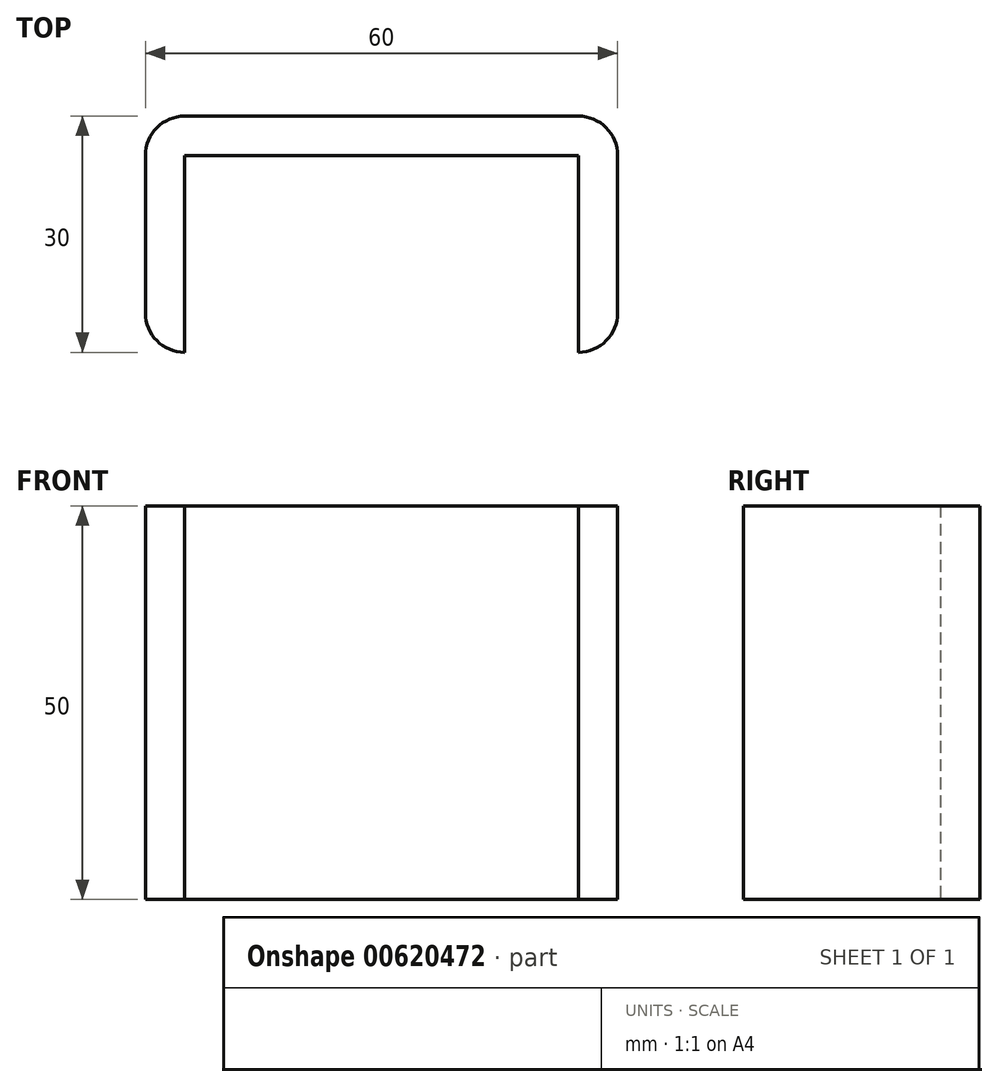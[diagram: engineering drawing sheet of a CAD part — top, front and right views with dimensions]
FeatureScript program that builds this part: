
annotation { "Feature Type Name" : "Feature", "Feature Type Description" : "" }
export const myFeature = defineFeature(function(context is Context, id is Id, definition is map)
    precondition{}
    {
        {
            var Q0;
            Q0=qCreatedBy(makeId("Top.planeOp"),FACE);
            var sketch = newSketch(context, id + "F0", { "sketchPlane" : qUnion([Q0])});
            skLineSegment(sketch, "E0.bottom", {"start": v(-30, 15) * mm, "end": v(30, 15) * mm});
            skLineSegment(sketch, "E0.top", {"start": v(-30, -15) * mm, "end": v(-25, -15) * mm});
            skLineSegment(sketch, "E0.left", {"start": v(-30, 15) * mm, "end": v(-30, -15) * mm});
            skLineSegment(sketch, "E0.right", {"start": v(30, 15) * mm, "end": v(30, -15) * mm});
            skPoint(sketch, "E0.middle", {"position": v(0, 0) * mm});
            skLineSegment(sketch, "E1.0", {"start": v(25, 10) * mm, "end": v(25, -15) * mm});
            skLineSegment(sketch, "E1.1", {"start": v(-25, 10) * mm, "end": v(25, 10) * mm});
            skLineSegment(sketch, "E1.2", {"start": v(-25, 10) * mm, "end": v(-25, -15) * mm});
            skLineSegment(sketch, "E2.trimOffspring", {"start": v(25, -15) * mm, "end": v(30, -15) * mm});
            skSolve(sketch);
        }
        {
            var Q0;
            Q0 = qSketchRegion(id + "F0", true);
            extrude(context, id + "F1", {"entities" : qUnion([Q0]), "depth" : 25 * mm, "offsetDistance" : 25 * mm, "hasSecondDirection" : true, "secondDirectionOppositeDirection" : true, "secondDirectionDepth" : 25 * mm});
        }
        {
            var Q0;
            Q0=makeQuery(id+"F1.opExtrude","SWEPT_EDGE",EDGE,{"disambiguationData":[OSD([sQuery(id+"F0.wireOp",EDGE,"E0.bottom"),sQuery(id+"F0.wireOp",EDGE,"E0.left")])]});
            var Q1;
            Q1=makeQuery(id+"F1.opExtrude","SWEPT_EDGE",EDGE,{"disambiguationData":[OSD([sQuery(id+"F0.wireOp",EDGE,"E0.bottom"),sQuery(id+"F0.wireOp",EDGE,"E0.right")])]});
            var Q2;
            Q2=makeQuery(id+"F1.opExtrude","SWEPT_EDGE",EDGE,{"disambiguationData":[OSD([sQuery(id+"F0.wireOp",EDGE,"E0.right"),sQuery(id+"F0.wireOp",EDGE,"E2.trimOffspring")])]});
            var Q3;
            Q3=makeQuery(id+"F1.opExtrude","SWEPT_EDGE",EDGE,{"disambiguationData":[OSD([sQuery(id+"F0.wireOp",EDGE,"E0.top"),sQuery(id+"F0.wireOp",EDGE,"E0.left")])]});
            fillet(context, id + "F2", {"entities" : qUnion([Q0, Q1, Q2, Q3]), "radius" : 5 * mm, "tangentPropagation" : true, "allowEdgeOverflow" : false});
        }
    });
